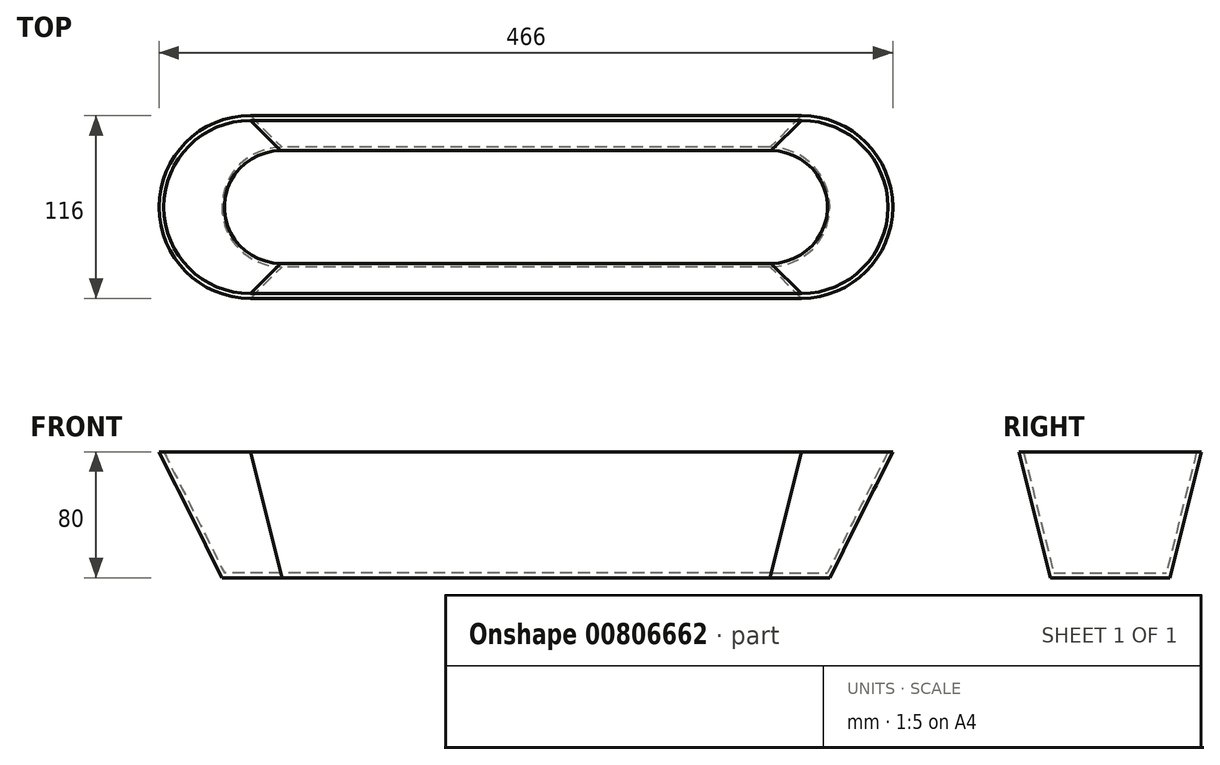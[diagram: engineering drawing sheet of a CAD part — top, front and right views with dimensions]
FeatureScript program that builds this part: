
annotation { "Feature Type Name" : "Feature", "Feature Type Description" : "" }
export const myFeature = defineFeature(function(context is Context, id is Id, definition is map)
    precondition{}
    {
        {
            var Q0;
            Q0=qCreatedBy(makeId("Top.planeOp"),FACE);
            cPlane(context, id + "F0", {"entities" : qUnion([Q0]), "cplaneType" : CPlaneType.OFFSET, "offset" : 80 * mm, "oppositeDirection" : true, "width" : 150 * mm, "height" : 150 * mm});
        }
        {
            var Q0;
            Q0=qCreatedBy(makeId("Top.planeOp"),FACE);
            var sketch = newSketch(context, id + "F1", { "sketchPlane" : qUnion([Q0])});
            skPoint(sketch, "E0.middle", {"position": v(0, 0) * mm});
            skLineSegment(sketch, "E1.bottom", {"start": v(175, 58) * mm, "end": v(-175, 58) * mm});
            skLineSegment(sketch, "E1.top", {"start": v(175, -58) * mm, "end": v(-175, -58) * mm});
            skArc(sketch, "E2", {"start": v(-175, 58) * mm, "mid": v(-233, 0) * mm, "end": v(-175, -58) * mm});
            skArc(sketch, "E3", {"start": v(175, -58) * mm, "mid": v(233, 0) * mm, "end": v(175, 58) * mm});
            skSolve(sketch);
        }
        {
            var Q0;
            Q0=qCreatedBy(id+"F0.planeOp",FACE);
            var sketch = newSketch(context, id + "F2", { "sketchPlane" : qUnion([Q0])});
            skPoint(sketch, "E4.middle", {"position": v(0, 0) * mm});
            skLineSegment(sketch, "E5.bottom", {"start": v(155, 38) * mm, "end": v(-155, 38) * mm});
            skLineSegment(sketch, "E5.top", {"start": v(155, -38) * mm, "end": v(-155, -38) * mm});
            skArc(sketch, "E6", {"start": v(-155, 38) * mm, "mid": v(-193, 0) * mm, "end": v(-155, -38) * mm});
            skArc(sketch, "E7", {"start": v(155, -38) * mm, "mid": v(193, 0) * mm, "end": v(155, 38) * mm});
            skSolve(sketch);
        }
        {
            var Q0;
            Q0 = qSketchRegion(id + "F1", true);
            var Q1;
            Q1 = qSketchRegion(id + "F2", true);
            loft(context, id + "F3", {"sheetProfilesArray" : [{ "sheetProfileEntities" : qUnion([Q0]) }, { "sheetProfileEntities" : qUnion([Q1]) }]});
        }
        {
            var Q0;
            Q0=qCreatedBy(makeId("Top.planeOp"),FACE);
            var sketch = newSketch(context, id + "F4", { "sketchPlane" : qUnion([Q0])});
            skArc(sketch, "E8", {"start": v(-175, 55) * mm, "mid": v(-230, 0) * mm, "end": v(-175, -55) * mm});
            skArc(sketch, "E9", {"start": v(175, -55) * mm, "mid": v(230, 0) * mm, "end": v(175, 55) * mm});
            skLineSegment(sketch, "E10.bottom", {"start": v(175, 55) * mm, "end": v(-175, 55) * mm});
            skLineSegment(sketch, "E10.top", {"start": v(175, -55) * mm, "end": v(-175, -55) * mm});
            skLineSegment(sketch, "E10.right", {"start": v(-175, 55) * mm, "end": v(-175, 55) * mm});
            skPoint(sketch, "E10.middle", {"position": v(0, 0) * mm});
            skLineSegment(sketch, "E11.trimOffspring", {"start": v(-175, -55) * mm, "end": v(-175, -55) * mm});
            skSolve(sketch);
        }
        {
            var Q0;
            Q0=qCreatedBy(id+"F0.planeOp",FACE);
            var sketch = newSketch(context, id + "F5", { "sketchPlane" : qUnion([Q0])});
            skLineSegment(sketch, "E12.bottom", {"start": v(155, -35) * mm, "end": v(-155, -35) * mm});
            skLineSegment(sketch, "E12.top", {"start": v(155, 35) * mm, "end": v(-155, 35) * mm});
            skPoint(sketch, "E12.middle", {"position": v(0, 0) * mm});
            skArc(sketch, "E13", {"start": v(-155, 35) * mm, "mid": v(-190, 0) * mm, "end": v(-155, -35) * mm});
            skArc(sketch, "E14", {"start": v(155, -35) * mm, "mid": v(190, 0) * mm, "end": v(155, 35) * mm});
            skSolve(sketch);
        }
        {
            var Q1;
            Q1 = qSketchRegion(id + "F4", true);
            var Q2;
            Q2 = qSketchRegion(id + "F5", true);
            loft(context, id + "F6", {"operationType" : NewBodyOperationType.REMOVE, "sheetProfilesArray" : [{ "sheetProfileEntities" : qUnion([Q1]) }, { "sheetProfileEntities" : qUnion([Q2]) }]});
        }
        {
            var Q0;
            Q0 = qSketchRegion(id + "F2", true);
            extrude(context, id + "F7", {"entities" : qUnion([Q0]), "operationType" : NewBodyOperationType.ADD, "depth" : 3 * mm, "offsetDistance" : 25 * mm});
        }
    });
